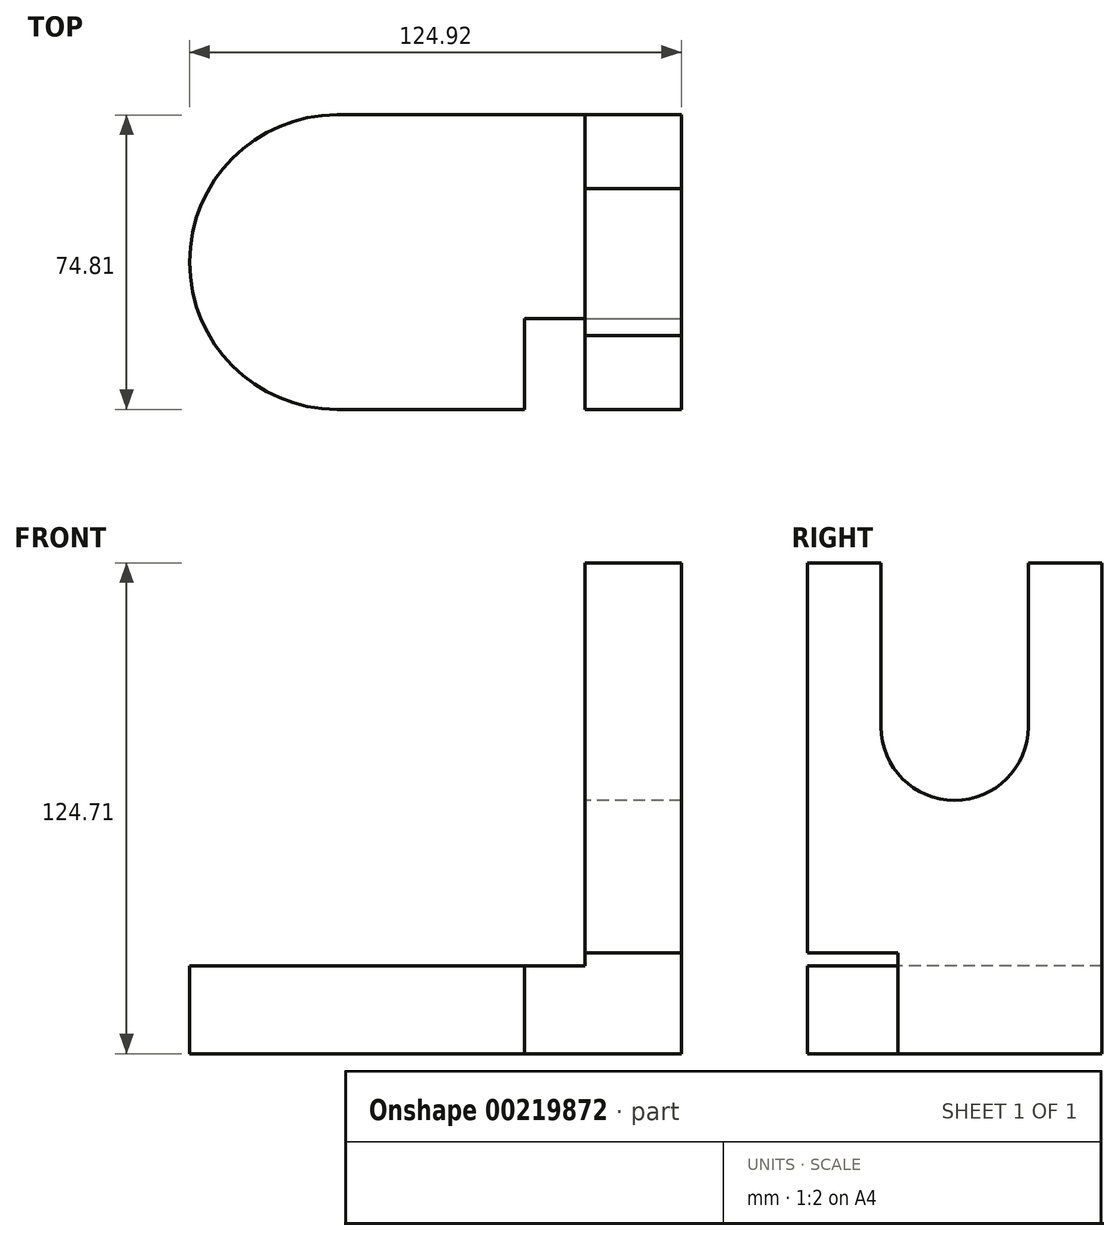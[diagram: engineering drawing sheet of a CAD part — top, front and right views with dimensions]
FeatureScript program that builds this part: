
annotation { "Feature Type Name" : "Feature", "Feature Type Description" : "" }
export const myFeature = defineFeature(function(context is Context, id is Id, definition is map)
    precondition{}
    {
        {
            var Q0;
            Q0=qCreatedBy(makeId("Top.planeOp"),FACE);
            var sketch = newSketch(context, id + "F0", { "sketchPlane" : qUnion([Q0])});
            skLineSegment(sketch, "E0", {"start": v(-46.87, 29.44) * mm, "end": v(40.64, 29.44) * mm});
            skLineSegment(sketch, "E1", {"start": v(40.64, 29.44) * mm, "end": v(40.64, -45.37) * mm});
            skLineSegment(sketch, "E2", {"start": v(40.64, -45.37) * mm, "end": v(-46.87, -45.37) * mm});
            skArc(sketch, "E3", {"start": v(-46.87, 29.44) * mm, "mid": v(-84.28, -7.97) * mm, "end": v(-46.87, -45.37) * mm});
            skSolve(sketch);
        }
        {
            var Q0;
            Q0=makeQuery(id+"F0.imprint","IMPRINT",FACE,{"disambiguationData":[TD([[makeQuery(id+"F0.imprint","IMPRINT",EDGE,{"derivedFrom":sQuery(id+"F0.wireOp",EDGE,"E0")}),-1.0]])]});
            extrude(context, id + "F1", {"entities" : qUnion([Q0]), "depth" : 124.7 * mm});
        }
        {
            var Q0;
            Q0=makeQuery(id+"F1.opExtrude","CAP_FACE",FACE,{"disambiguationData":[OSD([sQuery(id+"F0.wireOp",EDGE,"E0"),sQuery(id+"F0.wireOp",EDGE,"E1"),sQuery(id+"F0.wireOp",EDGE,"E2"),sQuery(id+"F0.wireOp",EDGE,"E3")])],"isStart":false});
            var sketch = newSketch(context, id + "F2", { "sketchPlane" : qUnion([Q0])});
            skLineSegment(sketch, "E4", {"start": v(16.19, 29.44) * mm, "end": v(16.19, -45.37) * mm});
            skLineSegment(sketch, "E5", {"start": v(16.19, -45.37) * mm, "end": v(-46.87, -45.37) * mm});
            skLineSegment(sketch, "E6", {"start": v(-46.87, 29.44) * mm, "end": v(16.19, 29.44) * mm});
            skArc(sketch, "E7", {"start": v(-46.87, 29.44) * mm, "mid": v(-84.28, -7.97) * mm, "end": v(-46.87, -45.37) * mm});
            skSolve(sketch);
        }
        {
            var Q0;
            Q0=makeQuery(id+"F2.imprint","IMPRINT",FACE,{"disambiguationData":[TD([[makeQuery(id+"F2.imprint","IMPRINT",EDGE,{"derivedFrom":sQuery(id+"F2.wireOp",EDGE,"E4")}),-1.0]])]});
            extrude(context, id + "F3", {"entities" : qUnion([Q0]), "operationType" : NewBodyOperationType.REMOVE, "oppositeDirection" : true, "depth" : 102.36 * mm});
        }
        {
            var Q0;
            Q0=makeQuery(id+"F3.boolean.opBoolean","COPY",FACE,{"derivedFrom":makeQuery(id+"F3.opExtrude","SWEPT_FACE",FACE,{"disambiguationData":[OSD([sQuery(id+"F2.wireOp",EDGE,"E4")])]})});
            var sketch = newSketch(context, id + "F4", { "sketchPlane" : qUnion([Q0])});
            skLineSegment(sketch, "E8", {"start": v(-10.74, 124.71) * mm, "end": v(-10.74, 83.05) * mm});
            skLineSegment(sketch, "E9.MirrorCS", {"start": v(26.67, 124.71) * mm, "end": v(26.67, 83.05) * mm});
            skLineSegment(sketch, "E10", {"start": v(-10.74, 124.71) * mm, "end": v(26.67, 124.71) * mm});
            skArc(sketch, "E11", {"start": v(-10.74, 83.05) * mm, "mid": v(7.97, 64.34) * mm, "end": v(26.67, 83.05) * mm});
            skSolve(sketch);
        }
        {
            var Q0;
            Q0=makeQuery(id+"F4.imprint","IMPRINT",FACE,{"disambiguationData":[TD([[makeQuery(id+"F4.imprint","IMPRINT",EDGE,{"derivedFrom":sQuery(id+"F4.wireOp",EDGE,"E8")}),1.0]])]});
            extrude(context, id + "F5", {"entities" : qUnion([Q0]), "operationType" : NewBodyOperationType.REMOVE, "oppositeDirection" : true, "depth" : 25.4 * mm});
        }
        {
            var Q0;
            Q0=makeQuery(id+"F1.opExtrude","SWEPT_FACE",FACE,{"disambiguationData":[OSD([sQuery(id+"F0.wireOp",EDGE,"E1")])]});
            var sketch = newSketch(context, id + "F6", { "sketchPlane" : qUnion([Q0])});
            skLineSegment(sketch, "E12", {"start": v(-45.37, 25.6) * mm, "end": v(-22.33, 25.6) * mm});
            skLineSegment(sketch, "E13", {"start": v(-22.33, 25.6) * mm, "end": v(-22.33, 0) * mm});
            skLineSegment(sketch, "E14", {"start": v(-22.33, 0) * mm, "end": v(-45.37, 0) * mm});
            skLineSegment(sketch, "E15", {"start": v(-45.37, 0) * mm, "end": v(-45.37, 25.6) * mm});
            skSolve(sketch);
        }
        {
            var Q0;
            Q0=makeQuery(id+"F6.imprint","IMPRINT",FACE,{"disambiguationData":[TD([[makeQuery(id+"F6.imprint","IMPRINT",EDGE,{"derivedFrom":sQuery(id+"F6.wireOp",EDGE,"E12")}),-1.0]])]});
            extrude(context, id + "F7", {"entities" : qUnion([Q0]), "operationType" : NewBodyOperationType.REMOVE, "oppositeDirection" : true, "depth" : 39.88 * mm});
        }
    });
